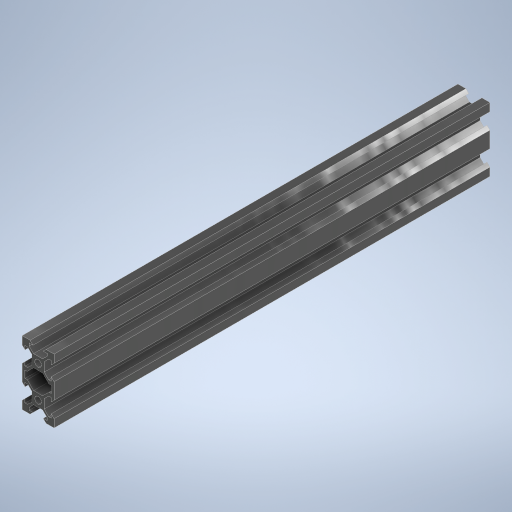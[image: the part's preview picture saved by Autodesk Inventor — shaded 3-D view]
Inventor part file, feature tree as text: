
AUTODESK INVENTOR PART (.ipt)
format: ipt  version: 2024.2 (Build 282272000, 272)  size: 415,232 bytes
history: native  units: mm
features: extrude x2, sketch x2, pattern_linear x1
ambient origin geometry x8: Origin, YZ Plane, XZ Plane, XY Plane, X Axis, Y Axis, Z Axis, Center Point
bodies: Solid1 (feature_tree)
feature tree (5):
  extrude  "ExtrusionModifier"  Depth=10.0mm
  pattern_linear  "Rectangular Pattern1"  Spacing1=4.4mm  [1 undecoded]
  extrude  "NoEdit"  TaperAngle=45.0deg  [1 undecoded]
  sketch  "Sketch1"  dims[d16=10.0mm d19=3.2mm]
  sketch  "Sketch2"  dims[d21=4.4mm d22=4.4mm d24=45.0deg d25=1.8mm d27=1.8mm d28=45.0deg d29=3.2mm d31=1.4mm d33=2.15mm d34=3.825mm d35=3.825mm d36=135.0deg d37=40.0mm d39=360.0deg d41=272.4mm d42=0.0mm d43=20.0mm d45=20.0mm d46=4.5mm d48=272.5mm d49=0.0mm d50=1.8mm d51=0.5mm d52=0.872665mm d53=0.5mm d54=0.872665mm]
note: 2 required parameter values undecoded (feature->parameter linkage not recoverable at this tier; creation-order binding heuristic only, values carry confidence <= 0.55)
